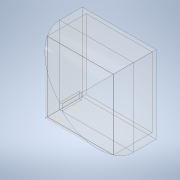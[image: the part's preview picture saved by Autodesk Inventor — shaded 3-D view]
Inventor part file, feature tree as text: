
AUTODESK INVENTOR PART (.ipt)
format: ipt  version: 2020 (Build 240168000, 168)  size: 142,336 bytes
history: native  units: mm
features: sketch x5, extrude x3, fillet x1
ambient origin geometry x8: Origin, YZ Plane, XZ Plane, XY Plane, X Axis, Y Axis, Z Axis, Center Point
bodies: Volumenkörper1 (feature_tree)
feature tree (9):
  extrude  "Extrusion1"  Depth=180.0mm
  sketch  "Skizze2"  dims[d2=10.0mm d3=10.0mm d4=10.0mm]
  extrude  "Extrusion2"  Depth=10.0mm
  fillet  "Rundung1"  Radius=10.0mm
  sketch  "Skizze4"  dims[d8=50.0mm d9=0.0mm]
  extrude  "Extrusion3"  Depth=100.0mm TaperAngle=0.0deg
  sketch  "Skizze1"  dims[d0=170.0mm d1=180.0mm]
  sketch  "Skizze3"  dims[d5=10.0mm d6=100.0mm d7=0.0mm]
  sketch  "Skizze5"  dims[d10=92.0mm d11=50.0mm d12=0.0mm]
